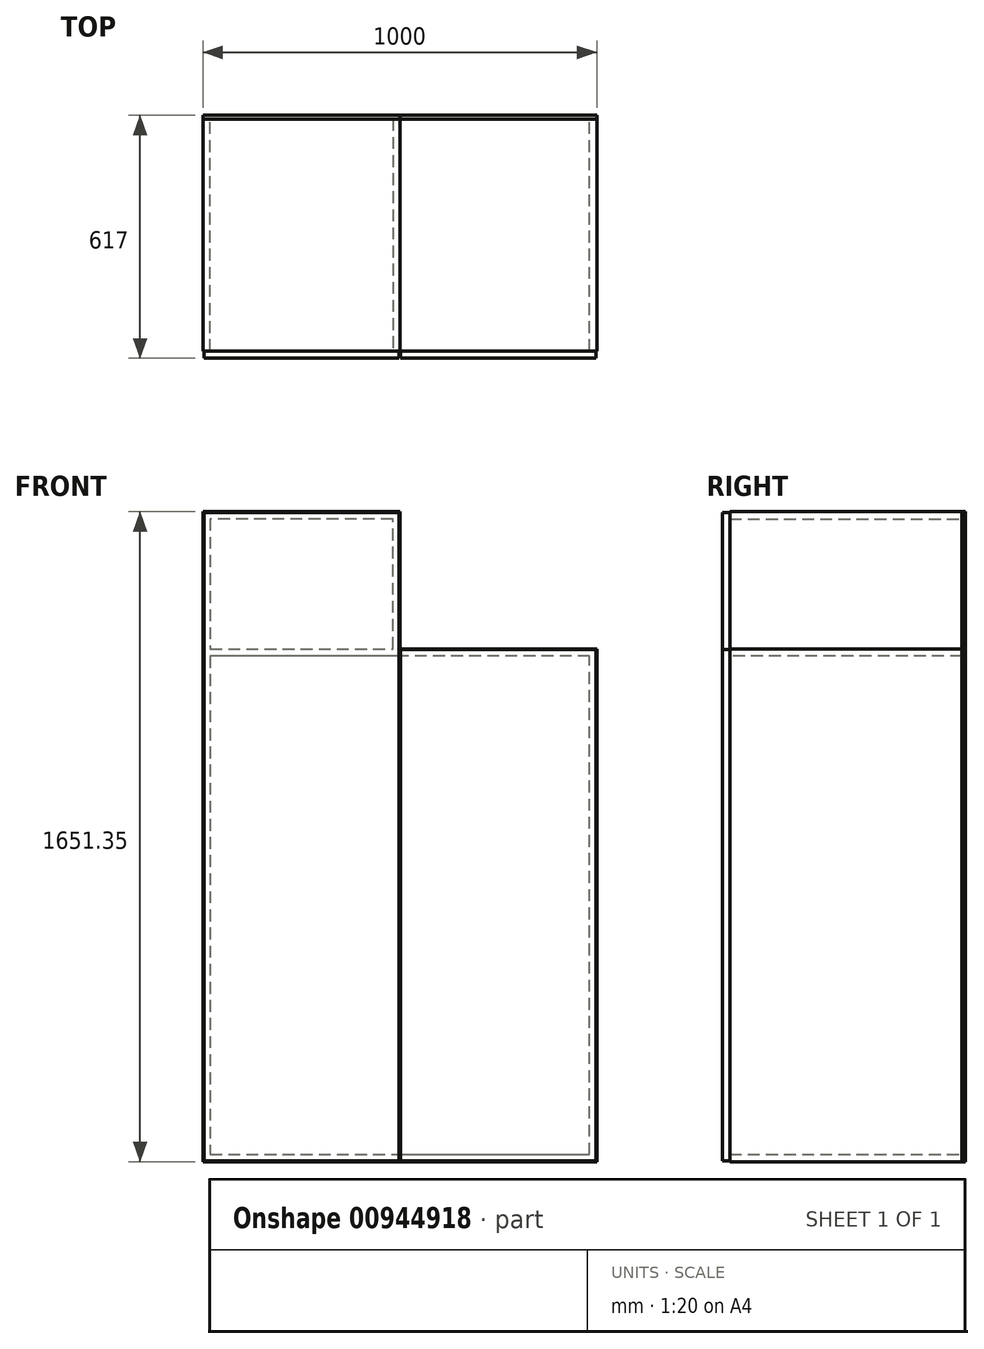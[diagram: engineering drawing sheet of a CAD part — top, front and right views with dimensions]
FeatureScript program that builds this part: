
annotation { "Feature Type Name" : "Feature", "Feature Type Description" : "" }
export const myFeature = defineFeature(function(context is Context, id is Id, definition is map)
    precondition{}
    {
        {
            var Q0;
            Q0=qCreatedBy(makeId("Front.planeOp"),FACE);
            var sketch = newSketch(context, id + "F0", { "sketchPlane" : qUnion([Q0])});
            skLineSegment(sketch, "E0", {"start": v(-2100, 2000) * mm, "end": v(0, 535.68) * mm, "construction": true});
            skLineSegment(sketch, "E1", {"start": v(0, 535.68) * mm, "end": v(0, 0) * mm, "construction": true});
            skLineSegment(sketch, "E2", {"start": v(-250, 0) * mm, "end": v(-250, 710) * mm, "construction": true});
            skLineSegment(sketch, "E3", {"start": v(-2100, 0) * mm, "end": v(-1100, 0) * mm});
            skLineSegment(sketch, "E4", {"start": v(-1100, 1302.7) * mm, "end": v(-1600, 1302.7) * mm});
            skLineSegment(sketch, "E5", {"start": v(-1600, 1302.7) * mm, "end": v(-1600, 1651.35) * mm});
            skLineSegment(sketch, "E6", {"start": v(-2100, 1651.35) * mm, "end": v(-2100, 0) * mm});
            skLineSegment(sketch, "E7", {"start": v(-1100, 0) * mm, "end": v(-1100, 1302.7) * mm});
            skLineSegment(sketch, "E8", {"start": v(-1600, 1651.35) * mm, "end": v(-2100, 1651.35) * mm});
            skLineSegment(sketch, "E9.0", {"start": v(-1618, 1284.7) * mm, "end": v(-1618, 1633.35) * mm});
            skLineSegment(sketch, "E9.1", {"start": v(-2082, 1633.35) * mm, "end": v(-2082, 18) * mm});
            skLineSegment(sketch, "E9.2", {"start": v(-2082, 18) * mm, "end": v(-1118, 18) * mm});
            skLineSegment(sketch, "E9.3", {"start": v(-1618, 1633.35) * mm, "end": v(-2082, 1633.35) * mm});
            skLineSegment(sketch, "E9.4", {"start": v(-1118, 18) * mm, "end": v(-1118, 1284.7) * mm});
            skLineSegment(sketch, "E9.5", {"start": v(-1118, 1284.7) * mm, "end": v(-1618, 1284.7) * mm});
            skSolve(sketch);
        }
        {
            var Q0;
            Q0 = qSketchRegion(id + "F0", true);
            extrude(context, id + "F1", {"entities" : qUnion([Q0]), "depth" : 590 * mm, "offsetDistance" : 25 * mm});
        }
        {
            var Q0;
            Q0=makeQuery(id+"F1.opExtrude","SWEPT_FACE",FACE,{"disambiguationData":[OSD([sQuery(id+"F0.wireOp",EDGE,"E9.0")])]});
            var sketch = newSketch(context, id + "F2", { "sketchPlane" : qUnion([Q0])});
            skLineSegment(sketch, "E10.bottom", {"start": v(0, 1284.7) * mm, "end": v(590, 1284.7) * mm});
            skLineSegment(sketch, "E10.top", {"start": v(0, 1302.7) * mm, "end": v(590, 1302.7) * mm});
            skLineSegment(sketch, "E10.left", {"start": v(0, 1284.7) * mm, "end": v(0, 1302.7) * mm});
            skLineSegment(sketch, "E10.right", {"start": v(590, 1284.7) * mm, "end": v(590, 1302.7) * mm});
            skSolve(sketch);
        }
        {
            var Q0;
            Q0 = qSketchRegion(id + "F2", true);
            extrude(context, id + "F3", {"entities" : qUnion([Q0]), "operationType" : NewBodyOperationType.ADD, "endBound" : BoundingType.UP_TO_NEXT, "depth" : 25 * mm, "offsetDistance" : 25 * mm});
        }
        {
            var Q0;
            Q0=makeQuery(id+"F3.boolean.opBoolean","MERGE",FACE,{"derivedFrom":[makeQuery(id+"F1.opExtrude","CAP_FACE",FACE,{"disambiguationData":[OSD([sQuery(id+"F0.wireOp",EDGE,"E3"),sQuery(id+"F0.wireOp",EDGE,"E4"),sQuery(id+"F0.wireOp",EDGE,"E5"),sQuery(id+"F0.wireOp",EDGE,"E6"),sQuery(id+"F0.wireOp",EDGE,"E7"),sQuery(id+"F0.wireOp",EDGE,"E8"),sQuery(id+"F0.wireOp",EDGE,"E9.0"),sQuery(id+"F0.wireOp",EDGE,"E9.1"),sQuery(id+"F0.wireOp",EDGE,"E9.2"),sQuery(id+"F0.wireOp",EDGE,"E9.3"),sQuery(id+"F0.wireOp",EDGE,"E9.4"),sQuery(id+"F0.wireOp",EDGE,"E9.5")])],"isStart":true}),makeQuery(id+"F3.opExtrude","SWEPT_FACE",FACE,{"disambiguationData":[OSD([sQuery(id+"F2.wireOp",EDGE,"E10.left")])]})]});
            var sketch = newSketch(context, id + "F4", { "sketchPlane" : qUnion([Q0])});
            skLineSegment(sketch, "E11", {"start": v(1100, 0) * mm, "end": v(1100, 1302.7) * mm});
            skLineSegment(sketch, "E12", {"start": v(1100, 1302.7) * mm, "end": v(1600, 1302.7) * mm});
            skLineSegment(sketch, "E13", {"start": v(1600, 1302.7) * mm, "end": v(1600, 1651.35) * mm});
            skLineSegment(sketch, "E14", {"start": v(1600, 1651.35) * mm, "end": v(2100, 1651.35) * mm});
            skLineSegment(sketch, "E15", {"start": v(2100, 1651.35) * mm, "end": v(2100, 0) * mm});
            skLineSegment(sketch, "E16", {"start": v(2100, 0) * mm, "end": v(1100, 0) * mm});
            skSolve(sketch);
        }
        {
            var Q0;
            Q0 = qSketchRegion(id + "F4", true);
            extrude(context, id + "F5", {"entities" : qUnion([Q0]), "depth" : 9 * mm, "offsetDistance" : 25 * mm});
        }
        {
            var Q0;
            Q0=makeQuery(id+"F3.boolean.opBoolean","MERGE",FACE,{"derivedFrom":[makeQuery(id+"F1.opExtrude","CAP_FACE",FACE,{"disambiguationData":[OSD([sQuery(id+"F0.wireOp",EDGE,"E3"),sQuery(id+"F0.wireOp",EDGE,"E4"),sQuery(id+"F0.wireOp",EDGE,"E5"),sQuery(id+"F0.wireOp",EDGE,"E6"),sQuery(id+"F0.wireOp",EDGE,"E7"),sQuery(id+"F0.wireOp",EDGE,"E8"),sQuery(id+"F0.wireOp",EDGE,"E9.0"),sQuery(id+"F0.wireOp",EDGE,"E9.1"),sQuery(id+"F0.wireOp",EDGE,"E9.2"),sQuery(id+"F0.wireOp",EDGE,"E9.3"),sQuery(id+"F0.wireOp",EDGE,"E9.4"),sQuery(id+"F0.wireOp",EDGE,"E9.5")])],"isStart":false}),makeQuery(id+"F3.opExtrude","SWEPT_FACE",FACE,{"disambiguationData":[OSD([sQuery(id+"F2.wireOp",EDGE,"E10.right")])]})]});
            var sketch = newSketch(context, id + "F6", { "sketchPlane" : qUnion([Q0])});
            skLineSegment(sketch, "E17.0", {"start": v(-1602, 1649.35) * mm, "end": v(-1602, 2) * mm});
            skLineSegment(sketch, "E17.1", {"start": v(-2098, 1649.35) * mm, "end": v(-1602, 1649.35) * mm});
            skLineSegment(sketch, "E17.2", {"start": v(-2098, 1649.35) * mm, "end": v(-2098, 2) * mm});
            skLineSegment(sketch, "E17.3", {"start": v(-2098, 2) * mm, "end": v(-1602, 2) * mm});
            skPoint(sketch, "E18.top.end.orphan", {"position": v(-1600, 0) * mm});
            skSolve(sketch);
        }
        {
            var Q0;
            Q0 = qSketchRegion(id + "F6", true);
            extrude(context, id + "F7", {"entities" : qUnion([Q0]), "depth" : 18 * mm, "offsetDistance" : 25 * mm});
        }
        {
            var Q0;
            Q0=makeQuery(id+"F3.boolean.opBoolean","MERGE",FACE,{"derivedFrom":[makeQuery(id+"F1.opExtrude","CAP_FACE",FACE,{"disambiguationData":[OSD([sQuery(id+"F0.wireOp",EDGE,"E3"),sQuery(id+"F0.wireOp",EDGE,"E4"),sQuery(id+"F0.wireOp",EDGE,"E5"),sQuery(id+"F0.wireOp",EDGE,"E6"),sQuery(id+"F0.wireOp",EDGE,"E7"),sQuery(id+"F0.wireOp",EDGE,"E8"),sQuery(id+"F0.wireOp",EDGE,"E9.0"),sQuery(id+"F0.wireOp",EDGE,"E9.1"),sQuery(id+"F0.wireOp",EDGE,"E9.2"),sQuery(id+"F0.wireOp",EDGE,"E9.3"),sQuery(id+"F0.wireOp",EDGE,"E9.4"),sQuery(id+"F0.wireOp",EDGE,"E9.5")])],"isStart":false}),makeQuery(id+"F3.opExtrude","SWEPT_FACE",FACE,{"disambiguationData":[OSD([sQuery(id+"F2.wireOp",EDGE,"E10.right")])]})]});
            var sketch = newSketch(context, id + "F8", { "sketchPlane" : qUnion([Q0])});
            skLineSegment(sketch, "E19.0", {"start": v(-1102, 1300.7) * mm, "end": v(-1598, 1300.7) * mm});
            skLineSegment(sketch, "E19.1", {"start": v(-1102, 2) * mm, "end": v(-1102, 1300.7) * mm});
            skLineSegment(sketch, "E19.2", {"start": v(-1102, 2) * mm, "end": v(-1598, 2) * mm});
            skLineSegment(sketch, "E19.3", {"start": v(-1598, 2) * mm, "end": v(-1598, 1300.7) * mm});
            skSolve(sketch);
        }
        {
            var Q0;
            Q0 = qSketchRegion(id + "F8", true);
            extrude(context, id + "F9", {"entities" : qUnion([Q0]), "depth" : 18 * mm, "offsetDistance" : 25 * mm});
        }
    });
